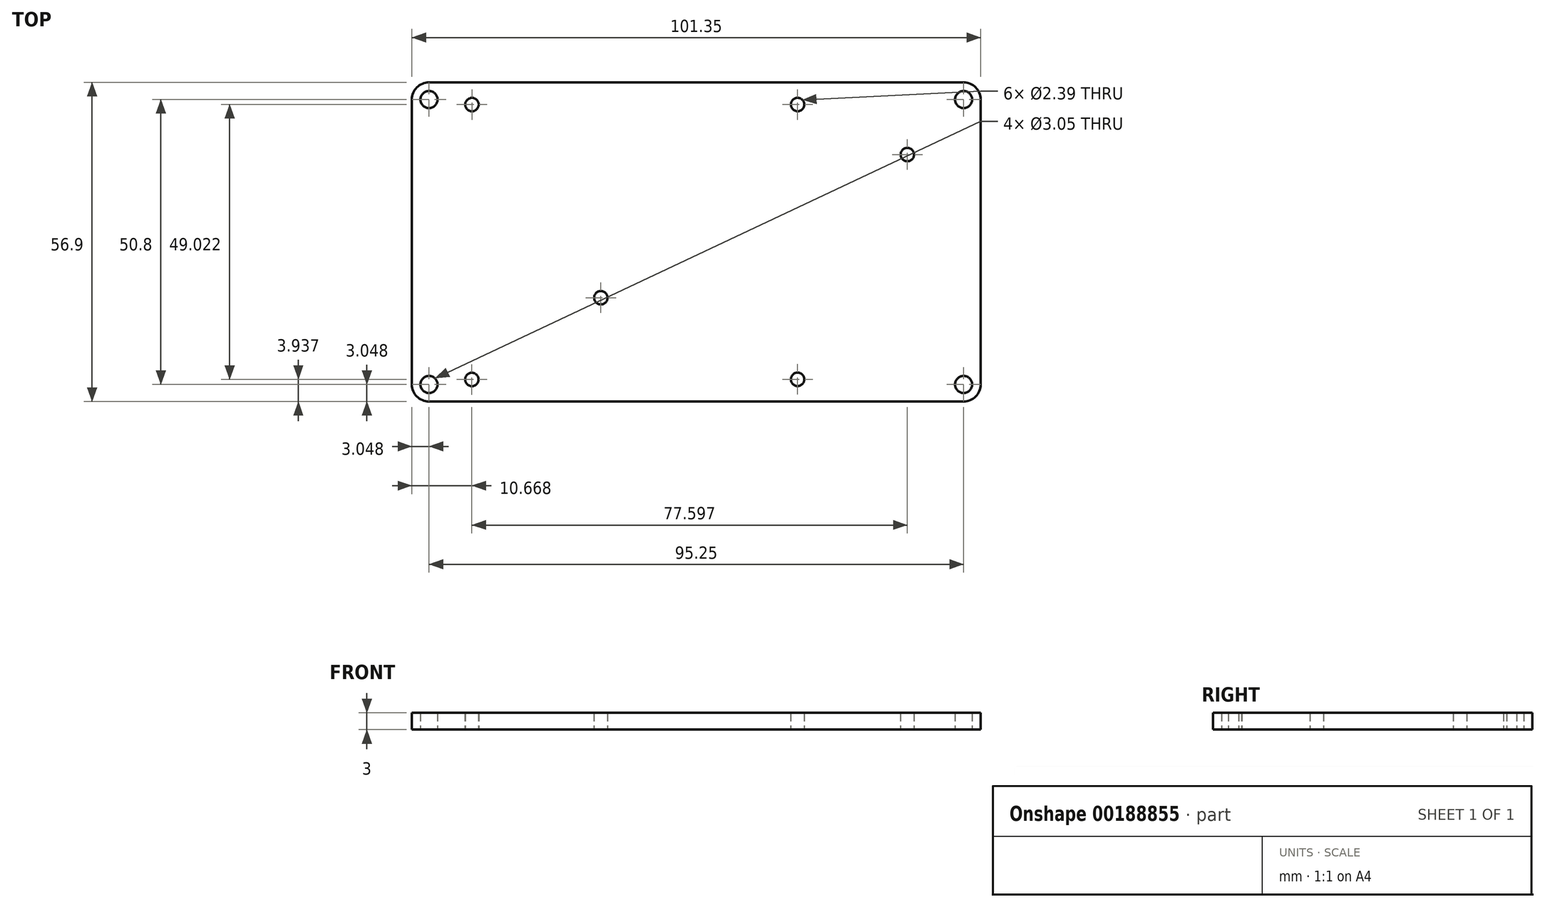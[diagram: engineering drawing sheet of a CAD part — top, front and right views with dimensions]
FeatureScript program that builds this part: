
annotation { "Feature Type Name" : "Feature", "Feature Type Description" : "" }
export const myFeature = defineFeature(function(context is Context, id is Id, definition is map)
    precondition{}
    {
        {
            var Q0;
            Q0=qCreatedBy(makeId("Top.planeOp"),FACE);
            var sketch = newSketch(context, id + "F0", { "sketchPlane" : qUnion([Q0])});
            skLineSegment(sketch, "E0.bottom", {"start": v(3.05, 0) * mm, "end": v(98.3, 0) * mm});
            skLineSegment(sketch, "E0.top", {"start": v(3.05, 56.9) * mm, "end": v(98.3, 56.9) * mm});
            skLineSegment(sketch, "E0.left", {"start": v(0, 3.05) * mm, "end": v(0, 53.85) * mm});
            skLineSegment(sketch, "E0.right", {"start": v(101.35, 3.05) * mm, "end": v(101.35, 53.85) * mm});
            skCircle(sketch, "E1", {"center": v(3.05, 3.05) * mm, "radius": 1.52 * mm});
            skCircle(sketch, "E2.0.1.0", {"center": v(3.05, 53.85) * mm, "radius": 1.52 * mm});
            skCircle(sketch, "E2.1.0.0", {"center": v(98.3, 3.05) * mm, "radius": 1.52 * mm});
            skCircle(sketch, "E2.1.1.0", {"center": v(98.3, 53.85) * mm, "radius": 1.52 * mm});
            skLineSegment(sketch, "E2.direction1", {"start": v(3.05, 3.05) * mm, "end": v(98.3, 3.05) * mm, "construction": true});
            skLineSegment(sketch, "E2.direction2", {"start": v(3.05, 3.05) * mm, "end": v(3.05, 53.85) * mm, "construction": true});
            skCircle(sketch, "E3", {"center": v(10.71, 52.96) * mm, "radius": 1.2 * mm});
            skCircle(sketch, "E4", {"center": v(10.67, 3.94) * mm, "radius": 1.2 * mm});
            skCircle(sketch, "E5", {"center": v(68.7, 3.95) * mm, "radius": 1.2 * mm});
            skCircle(sketch, "E6", {"center": v(68.7, 52.96) * mm, "radius": 1.2 * mm});
            skCircle(sketch, "E7", {"center": v(33.66, 18.5) * mm, "radius": 1.2 * mm});
            skCircle(sketch, "E8", {"center": v(88.27, 44.04) * mm, "radius": 1.2 * mm});
            skPoint(sketch, "E9.visualSharp", {"position": v(101.35, 56.9) * mm});
            skArc(sketch, "E9.filletArc", {"start": v(101.35, 53.85) * mm, "mid": v(100.45, 56) * mm, "end": v(98.3, 56.9) * mm});
            skPoint(sketch, "E10.visualSharp", {"position": v(101.35, 0) * mm});
            skArc(sketch, "E10.filletArc", {"start": v(98.3, 0) * mm, "mid": v(100.45, 0.9) * mm, "end": v(101.35, 3.05) * mm});
            skPoint(sketch, "E11.visualSharp", {"position": v(0, 0) * mm});
            skArc(sketch, "E11.filletArc", {"start": v(0, 3.05) * mm, "mid": v(0.9, 0.9) * mm, "end": v(3.05, 0) * mm});
            skPoint(sketch, "E12.visualSharp", {"position": v(0, 56.9) * mm});
            skArc(sketch, "E12.filletArc", {"start": v(3.05, 56.9) * mm, "mid": v(0.9, 56) * mm, "end": v(0, 53.85) * mm});
            skSolve(sketch);
        }
        {
            var Q0;
            Q0 = qSketchRegion(id + "F0", true);
            extrude(context, id + "F1", {"entities" : qUnion([Q0]), "depth" : 3 * mm});
        }
    });
